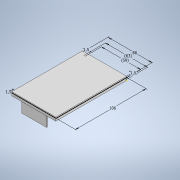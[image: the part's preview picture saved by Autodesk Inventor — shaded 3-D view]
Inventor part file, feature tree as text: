
AUTODESK INVENTOR PART (.ipt)
format: ipt  version: 2020 (Build 240168000, 168)  size: 148,480 bytes
history: native  units: mm
features: sketch x7, extrude x5
ambient origin geometry x8: Origin, YZ Plane, XZ Plane, XY Plane, X Axis, Y Axis, Z Axis, Center Point
bodies: Volumenkörper1 (feature_tree)
feature tree (12):
  sketch  "Skizze1"  dims[d0=106.0mm d1=66.0mm]
  extrude  "Extrusion1"  Depth=66.0mm
  extrude  "Extrusion2"  Depth=1.5mm
  extrude  "Extrusion3"  Depth=1.5mm TaperAngle=0.0deg
  sketch  "Skizze3"  dims[d4=1.5mm d5=1.5mm d6=0.0mm]
  sketch  "Skizze4"  dims[d7=1.5mm d8=4.0mm d9=0.0mm d10=0.0mm d11=106.0mm]
  extrude  "Extrusion4"  Depth=106.0mm
  sketch  "Skizze6"  dims[d15=106.0mm]
  extrude  "Extrusion5"  Depth=2.0mm TaperAngle=0.0deg
  sketch  "Skizze2"  dims[d2=1.5mm d3=1.5mm]
  sketch  "Skizze5"  dims[d12=1.5mm d13=2.0mm d14=0.0mm]
  sketch  "Skizze7"  dims[d16=1.5mm d17=2.5mm d18=2.0mm d19=0.0mm d20=59.0mm d21=63.0mm d22=37.0mm d23=66.0mm d24=15.0mm d25=15.0mm d26=0.0mm d27=0.5mm d28=0.872665mm d29=0.5mm d30=0.872665mm]
